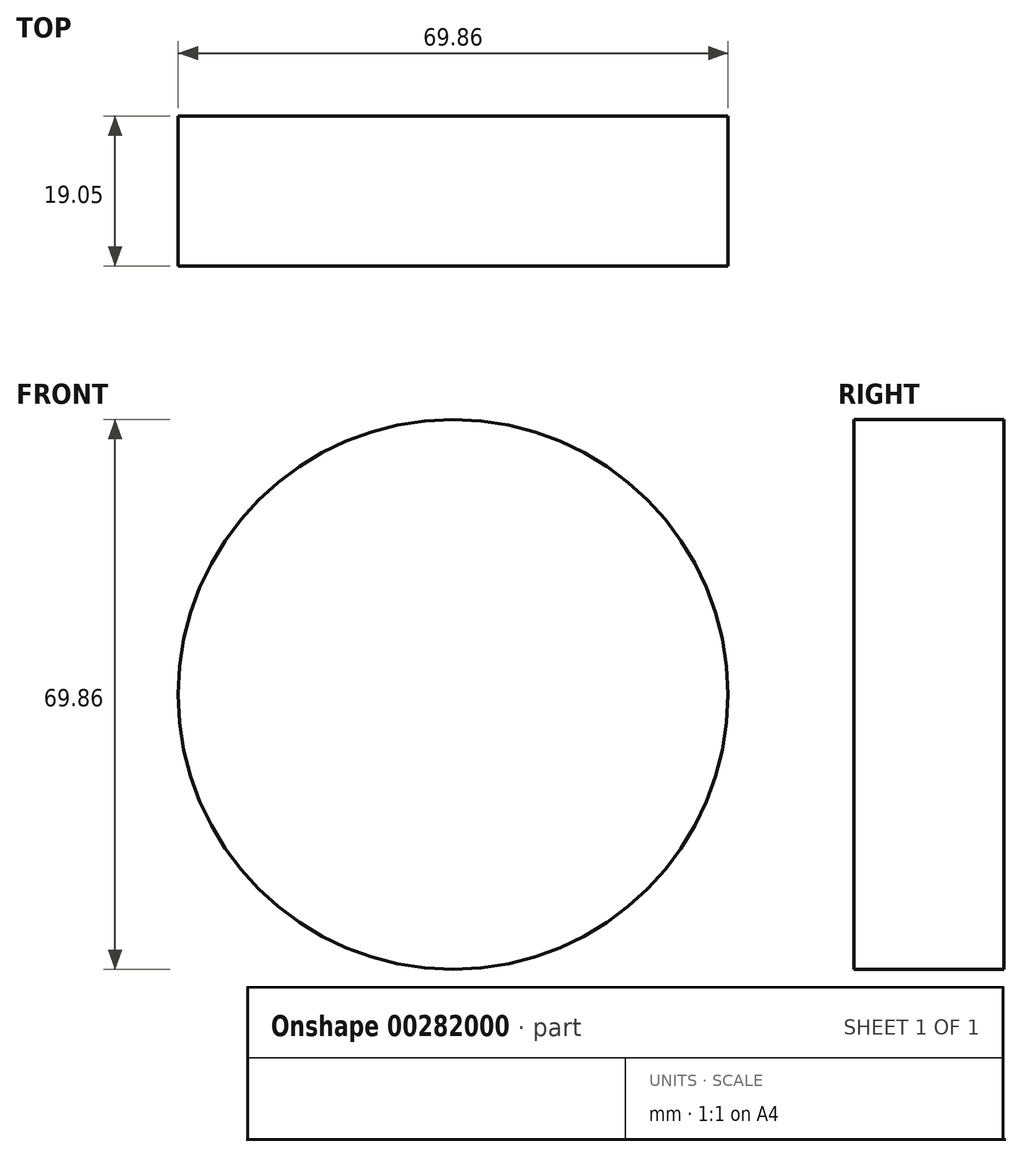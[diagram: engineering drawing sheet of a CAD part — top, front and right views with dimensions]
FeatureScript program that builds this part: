
annotation { "Feature Type Name" : "Feature", "Feature Type Description" : "" }
export const myFeature = defineFeature(function(context is Context, id is Id, definition is map)
    precondition{}
    {
        {
            var Q0;
            Q0=qCreatedBy(makeId("Front.planeOp"),FACE);
            var sketch = newSketch(context, id + "F0", { "sketchPlane" : qUnion([Q0])});
            skCircle(sketch, "E0", {"center": v(0, 0) * mm, "radius": 34.93 * mm});
            skSolve(sketch);
        }
        {
            var Q0;
            Q0=makeQuery(id+"F0.imprint","IMPRINT",FACE,{"disambiguationData":[TD([[makeQuery(id+"F0.imprint","IMPRINT",EDGE,{"derivedFrom":sQuery(id+"F0.wireOp",EDGE,"E0")}),1.0]])]});
            extrude(context, id + "F1", {"entities" : qUnion([Q0]), "depth" : 19.05 * mm});
        }
    });
